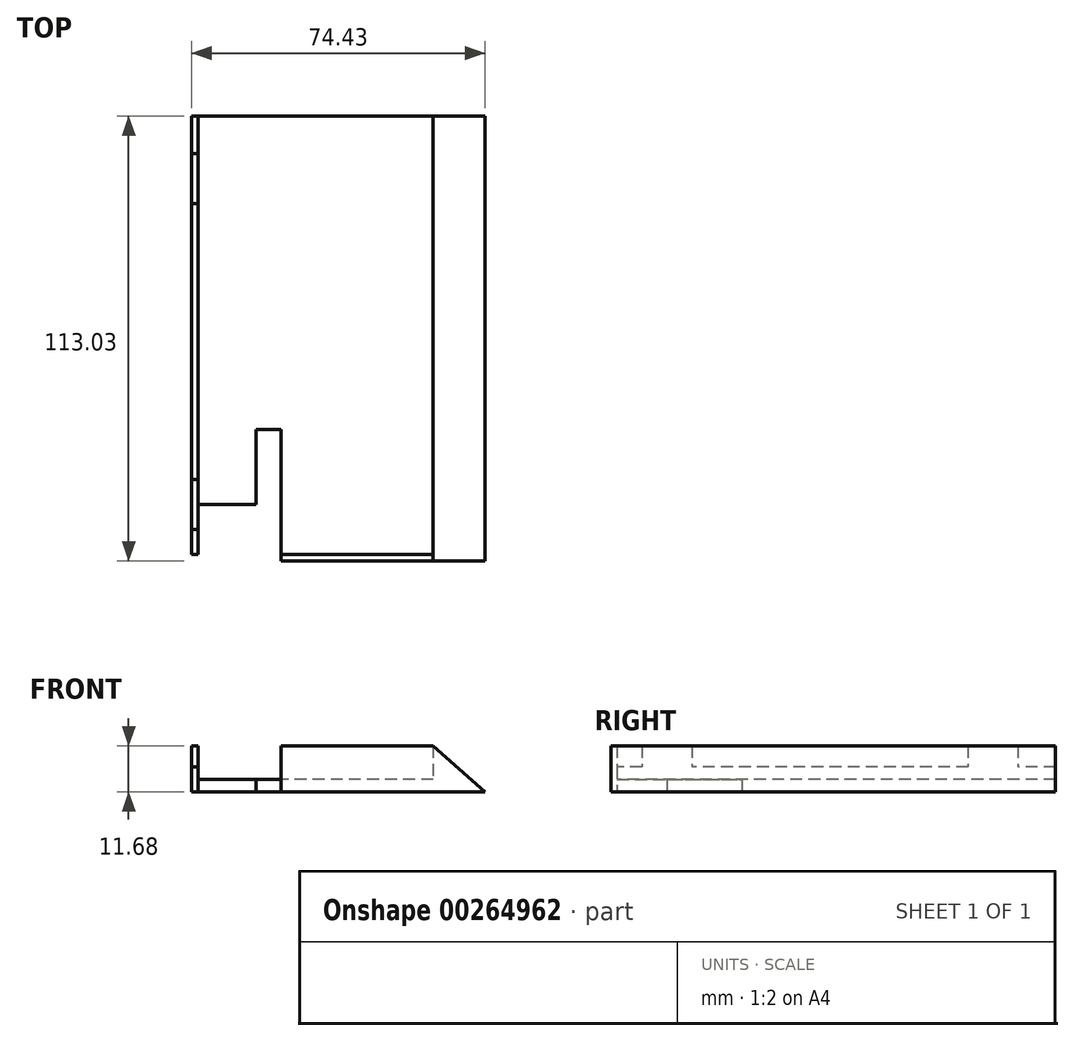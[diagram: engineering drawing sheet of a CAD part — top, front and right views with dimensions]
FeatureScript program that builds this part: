
annotation { "Feature Type Name" : "Feature", "Feature Type Description" : "" }
export const myFeature = defineFeature(function(context is Context, id is Id, definition is map)
    precondition{}
    {
        {
            var Q0;
            Q0=qCreatedBy(makeId("Top.planeOp"),FACE);
            var sketch = newSketch(context, id + "F0", { "sketchPlane" : qUnion([Q0])});
            skLineSegment(sketch, "E0.bottom", {"start": v(29.87, 55.72) * mm, "end": v(-29.87, 55.72) * mm});
            skLineSegment(sketch, "E0.top", {"start": v(29.87, -55.72) * mm, "end": v(-29.87, -55.72) * mm});
            skLineSegment(sketch, "E0.left", {"start": v(29.87, 55.72) * mm, "end": v(29.87, -55.72) * mm});
            skLineSegment(sketch, "E0.right", {"start": v(-29.87, 55.72) * mm, "end": v(-29.87, -55.72) * mm});
            skPoint(sketch, "E0.middle", {"position": v(0, 0) * mm});
            skLineSegment(sketch, "E1.bottom", {"start": v(29.87, 55.72) * mm, "end": v(42.97, 55.72) * mm});
            skLineSegment(sketch, "E1.top", {"start": v(29.87, -55.72) * mm, "end": v(42.97, -55.72) * mm});
            skLineSegment(sketch, "E1.right", {"start": v(42.97, 55.72) * mm, "end": v(42.97, -55.72) * mm});
            skLineSegment(sketch, "E2.top", {"start": v(-29.87, -43.02) * mm, "end": v(-8.81, -43.02) * mm});
            skLineSegment(sketch, "E2.right", {"start": v(-8.81, -55.72) * mm, "end": v(-8.81, -43.02) * mm});
            skLineSegment(sketch, "E3.bottom", {"start": v(-8.81, -55.72) * mm, "end": v(42.97, -55.72) * mm});
            skLineSegment(sketch, "E3.top", {"start": v(-8.81, -57.3) * mm, "end": v(42.97, -57.3) * mm});
            skLineSegment(sketch, "E3.left", {"start": v(-8.81, -55.72) * mm, "end": v(-8.81, -57.3) * mm});
            skLineSegment(sketch, "E3.right", {"start": v(42.97, -55.72) * mm, "end": v(42.97, -57.3) * mm});
            skLineSegment(sketch, "E4.bottom", {"start": v(-29.87, 55.72) * mm, "end": v(-31.46, 55.72) * mm});
            skLineSegment(sketch, "E4.top", {"start": v(-29.87, -55.72) * mm, "end": v(-31.46, -55.72) * mm});
            skLineSegment(sketch, "E4.right", {"start": v(-31.46, 55.72) * mm, "end": v(-31.46, -55.72) * mm});
            skLineSegment(sketch, "E5.bottom", {"start": v(-8.81, -43.02) * mm, "end": v(-15.16, -43.02) * mm});
            skLineSegment(sketch, "E5.top", {"start": v(-8.81, -23.97) * mm, "end": v(-15.16, -23.97) * mm});
            skLineSegment(sketch, "E5.left", {"start": v(-8.81, -43.02) * mm, "end": v(-8.81, -23.97) * mm});
            skLineSegment(sketch, "E5.right", {"start": v(-15.16, -43.02) * mm, "end": v(-15.16, -23.97) * mm});
            skSolve(sketch);
        }
        {
            var Q0;
            {var subQ3=sQuery(id+"F0.wireOp",EDGE,"E0.bottom");Q0=makeQuery(id+"F0.imprint","IMPRINT",FACE,{"disambiguationData":[TD([[makeQuery(id+"F0.imprint","IMPRINT",EDGE,{"derivedFrom":subQ3}),1.0]])]});}
            extrude(context, id + "F1", {"entities" : qUnion([Q0]), "depth" : 3.17 * mm, "offsetDistance" : 25.4 * mm});
        }
        {
            var Q0;
            {var subQ3=sQuery(id+"F0.wireOp",EDGE,"E4.bottom");Q0=makeQuery(id+"F0.imprint","IMPRINT",FACE,{"disambiguationData":[TD([[makeQuery(id+"F0.imprint","IMPRINT",EDGE,{"derivedFrom":subQ3}),1.0]])]});}
            extrude(context, id + "F2", {"entities" : qUnion([Q0]), "operationType" : NewBodyOperationType.ADD, "depth" : 6.35 * mm, "offsetDistance" : 25.4 * mm});
        }
        {
            var Q0;
            Q0=makeQuery(id+"F0.imprint","IMPRINT",FACE,{"disambiguationData":[TD([[makeQuery(id+"F0.imprint","IMPRINT",EDGE,{"derivedFrom":sQuery(id+"F0.wireOp",EDGE,"E3.top")}),1.0]])]});
            var Q1;
            Q1=makeQuery(id+"F0.imprint","IMPRINT",FACE,{"disambiguationData":[TD([[makeQuery(id+"F0.imprint","IMPRINT",EDGE,{"derivedFrom":sQuery(id+"F0.wireOp",EDGE,"E1.bottom")}),-1.0]])]});
            extrude(context, id + "F3", {"entities" : qUnion([Q0, Q1]), "operationType" : NewBodyOperationType.ADD, "depth" : 11.68 * mm, "offsetDistance" : 25.4 * mm});
        }
        {
            var Q0;
            Q0=makeQuery(id+"F3.boolean.opBoolean","MERGE",FACE,{"derivedFrom":[makeQuery(id+"F2.boolean.opBoolean","MERGE",FACE,{"derivedFrom":[makeQuery(id+"F1.opExtrude","SWEPT_FACE",FACE,{"disambiguationData":[OSD([sQuery(id+"F0.wireOp",EDGE,"E0.bottom")])]}),makeQuery(id+"F2.opExtrude","SWEPT_FACE",FACE,{"disambiguationData":[OSD([sQuery(id+"F0.wireOp",EDGE,"E4.bottom")])]})]}),makeQuery(id+"F3.opExtrude","SWEPT_FACE",FACE,{"disambiguationData":[OSD([sQuery(id+"F0.wireOp",EDGE,"E1.bottom")])]})]});
            var sketch = newSketch(context, id + "F4", { "sketchPlane" : qUnion([Q0])});
            skLineSegment(sketch, "E6", {"start": v(-29.87, 11.68) * mm, "end": v(-42.97, 0) * mm});
            skSolve(sketch);
        }
        {
            var Q0;
            Q0=makeQuery(id+"F4.imprint","IMPRINT",FACE,{"disambiguationData":[TD([[makeQuery(id+"F4.imprint","IMPRINT",EDGE,{"derivedFrom":sQuery(id+"F4.wireOp",EDGE,"E6")}),-1.0]])]});
            var Q1;
            Q1=makeQuery(id+"F3.opExtrude","SWEPT_FACE",FACE,{"disambiguationData":[OSD([sQuery(id+"F0.wireOp",EDGE,"E3.top")])]});
            extrude(context, id + "F5", {"entities" : qUnion([Q0]), "operationType" : NewBodyOperationType.REMOVE, "endBound" : BoundingType.UP_TO_SURFACE, "oppositeDirection" : true, "depth" : 25.4 * mm, "endBoundEntityFace" : qUnion([Q1]), "offsetDistance" : 25.4 * mm});
        }
        {
            var Q0;
            Q0=makeQuery(id+"F2.opExtrude","CAP_FACE",FACE,{"disambiguationData":[OSD([sQuery(id+"F0.wireOp",EDGE,"E4.bottom"),sQuery(id+"F0.wireOp",EDGE,"E4.top"),sQuery(id+"F0.wireOp",EDGE,"E0.right"),sQuery(id+"F0.wireOp",EDGE,"E4.right")])],"isStart":false});
            var sketch = newSketch(context, id + "F6", { "sketchPlane" : qUnion([Q0])});
            skLineSegment(sketch, "E7.bottom", {"start": v(-31.46, -49.37) * mm, "end": v(-29.87, -49.37) * mm});
            skLineSegment(sketch, "E7.top", {"start": v(-31.46, -36.67) * mm, "end": v(-29.87, -36.67) * mm});
            skLineSegment(sketch, "E7.left", {"start": v(-31.46, -49.37) * mm, "end": v(-31.46, -36.67) * mm});
            skLineSegment(sketch, "E7.right", {"start": v(-29.87, -49.37) * mm, "end": v(-29.87, -36.67) * mm});
            skLineSegment(sketch, "E8.bottom", {"start": v(-31.46, 46.2) * mm, "end": v(-29.87, 46.2) * mm});
            skLineSegment(sketch, "E8.top", {"start": v(-31.46, 33.5) * mm, "end": v(-29.87, 33.5) * mm});
            skLineSegment(sketch, "E8.left", {"start": v(-31.46, 46.2) * mm, "end": v(-31.46, 33.5) * mm});
            skLineSegment(sketch, "E8.right", {"start": v(-29.87, 46.2) * mm, "end": v(-29.87, 33.5) * mm});
            skSolve(sketch);
        }
        {
            var Q0;
            Q0=makeQuery(id+"F6.imprint","IMPRINT",FACE,{"disambiguationData":[TD([[makeQuery(id+"F6.imprint","IMPRINT",EDGE,{"derivedFrom":sQuery(id+"F6.wireOp",EDGE,"E8.bottom")}),-1.0]])]});
            var Q1;
            Q1=makeQuery(id+"F6.imprint","IMPRINT",FACE,{"disambiguationData":[TD([[makeQuery(id+"F6.imprint","IMPRINT",EDGE,{"derivedFrom":sQuery(id+"F6.wireOp",EDGE,"E7.bottom")}),1.0]])]});
            var Q2;
            Q2=makeQuery(id+"F3.opExtrude","CAP_VERTEX",VERTEX,{"disambiguationData":[OSD([sQuery(id+"F0.wireOp",EDGE,"E3.top"),sQuery(id+"F0.wireOp",EDGE,"E3.left")])],"isStart":false});
            extrude(context, id + "F7", {"entities" : qUnion([Q0, Q1]), "operationType" : NewBodyOperationType.ADD, "endBound" : BoundingType.UP_TO_VERTEX, "depth" : 25.4 * mm, "endBoundEntityVertex" : qUnion([Q2]), "offsetDistance" : 25.4 * mm});
        }
    });
